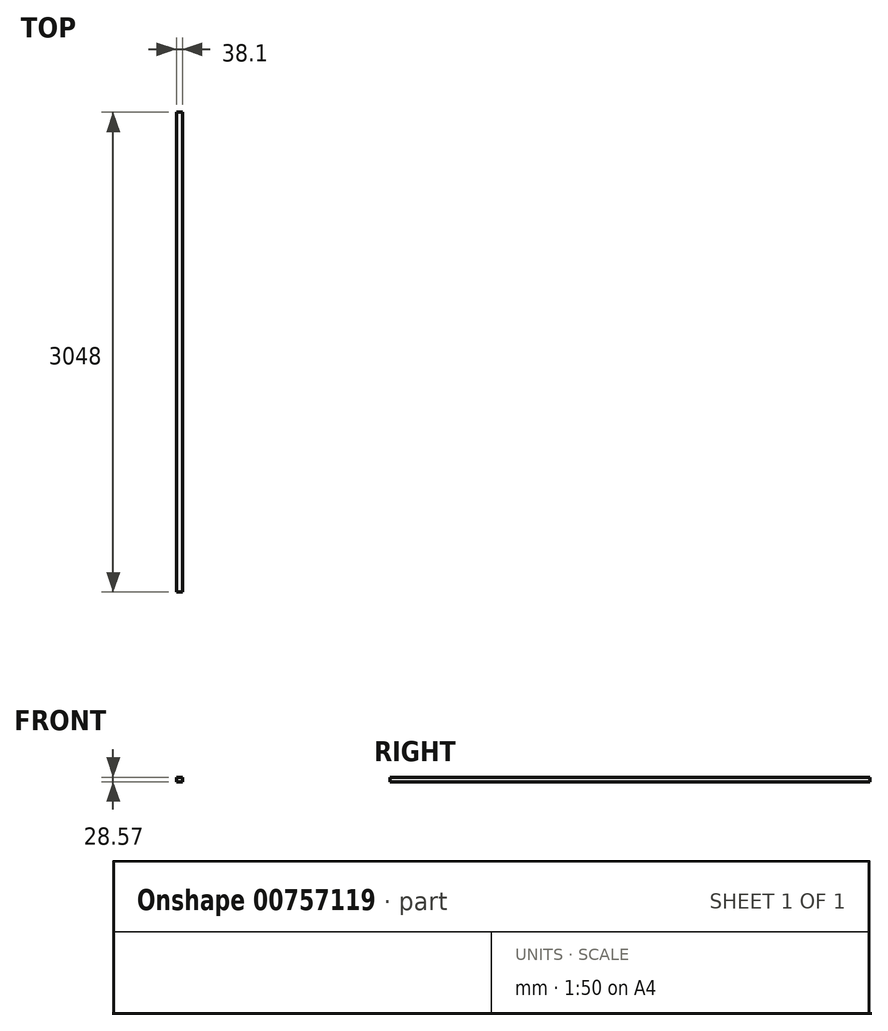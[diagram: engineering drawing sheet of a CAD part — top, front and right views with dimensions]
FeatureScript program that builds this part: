
annotation { "Feature Type Name" : "Feature", "Feature Type Description" : "" }
export const myFeature = defineFeature(function(context is Context, id is Id, definition is map)
    precondition{}
    {
        {
            var Q0;
            Q0=qCreatedBy(makeId("Front.planeOp"),FACE);
            var sketch = newSketch(context, id + "F0", { "sketchPlane" : qUnion([Q0])});
            skLineSegment(sketch, "E0.bottom", {"start": v(0, 0) * mm, "end": v(38.1, 0) * mm});
            skLineSegment(sketch, "E0.top", {"start": v(0, 28.58) * mm, "end": v(38.1, 28.58) * mm});
            skLineSegment(sketch, "E0.left", {"start": v(0, 0) * mm, "end": v(0, 28.58) * mm});
            skLineSegment(sketch, "E0.right", {"start": v(38.1, 0) * mm, "end": v(38.1, 28.58) * mm});
            skSolve(sketch);
        }
        {
            var Q0;
            Q0=makeQuery(id+"F0.imprint","IMPRINT",FACE,{"disambiguationData":[TD([[makeQuery(id+"F0.imprint","IMPRINT",EDGE,{"derivedFrom":sQuery(id+"F0.wireOp",EDGE,"E0.bottom")}),1.0]])]});
            extrude(context, id + "F1", {"entities" : qUnion([Q0]), "depth" : 3048 * mm, "offsetDistance" : 25.4 * mm});
        }
    });
